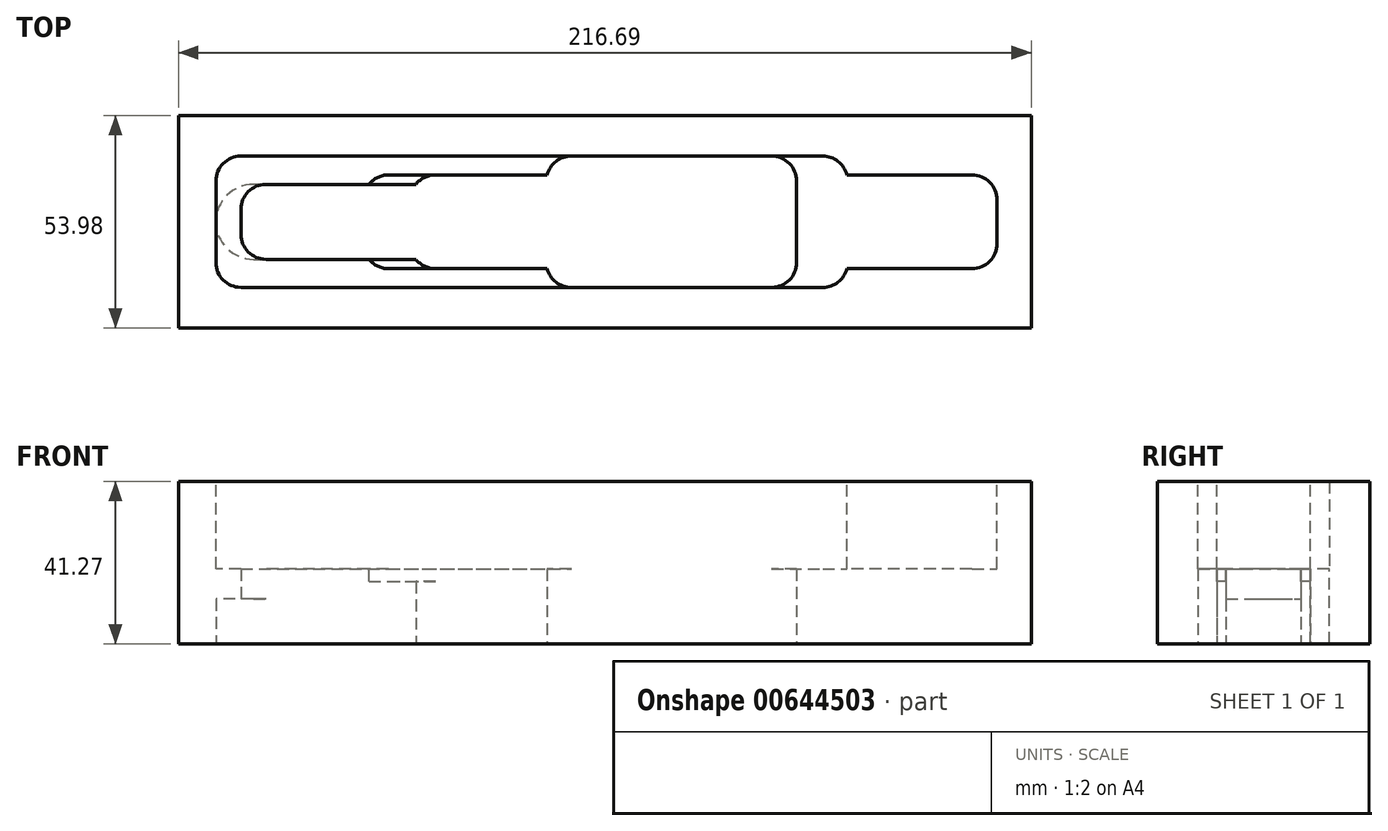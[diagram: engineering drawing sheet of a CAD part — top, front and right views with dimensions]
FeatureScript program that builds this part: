
annotation { "Feature Type Name" : "Feature", "Feature Type Description" : "" }
export const myFeature = defineFeature(function(context is Context, id is Id, definition is map)
    precondition{}
    {
        {
            var Q0;
            Q0=qCreatedBy(makeId("Top.planeOp"),FACE);
            var sketch = newSketch(context, id + "F0", { "sketchPlane" : qUnion([Q0])});
            skLineSegment(sketch, "E0.bottom", {"start": v(127, 26.99) * mm, "end": v(-127, 26.99) * mm});
            skLineSegment(sketch, "E0.top", {"start": v(127, -26.99) * mm, "end": v(-127, -26.99) * mm});
            skLineSegment(sketch, "E0.left", {"start": v(127, 26.99) * mm, "end": v(127, -26.99) * mm});
            skLineSegment(sketch, "E0.right", {"start": v(-127, 26.99) * mm, "end": v(-127, -26.99) * mm});
            skPoint(sketch, "E0.middle", {"position": v(0, 0) * mm});
            skSolve(sketch);
        }
        {
            var Q0;
            Q0=qSketchRegion(id+"F0",true);
            extrude(context, id + "F1", {"entities" : qUnion([Q0]), "depth" : 41.27 * mm});
        }
        {
            var Q0;
            Q0=makeQuery(id+"F1.opExtrude","CAP_FACE",FACE,{"disambiguationData":[OSD([sQuery(id+"F0.wireOp",EDGE,"E0.bottom"),sQuery(id+"F0.wireOp",EDGE,"E0.top"),sQuery(id+"F0.wireOp",EDGE,"E0.left"),sQuery(id+"F0.wireOp",EDGE,"E0.right")])],"isStart":false});
            var sketch = newSketch(context, id + "F2", { "sketchPlane" : qUnion([Q0])});
            skLineSegment(sketch, "E1.bottom", {"start": v(-80.17, -16.67) * mm, "end": v(80.17, -16.67) * mm});
            skLineSegment(sketch, "E1.top", {"start": v(-80.17, 16.67) * mm, "end": v(80.17, 16.67) * mm});
            skLineSegment(sketch, "E1.left", {"start": v(-80.17, -16.67) * mm, "end": v(-80.17, 16.67) * mm});
            skPoint(sketch, "E1.middle", {"position": v(0, 0) * mm});
            skLineSegment(sketch, "E2", {"start": v(80.17, 16.67) * mm, "end": v(80.17, 11.9) * mm});
            skLineSegment(sketch, "E3", {"start": v(80.17, 11.9) * mm, "end": v(118.27, 11.9) * mm});
            skLineSegment(sketch, "E4", {"start": v(118.27, 11.9) * mm, "end": v(118.27, -11.9) * mm});
            skLineSegment(sketch, "E5", {"start": v(118.27, -11.9) * mm, "end": v(80.17, -11.9) * mm});
            skLineSegment(sketch, "E6", {"start": v(80.17, -11.9) * mm, "end": v(80.17, -16.67) * mm});
            skSolve(sketch);
        }
        {
            var Q0;
            Q0=qSketchRegion(id+"F2",true);
            extrude(context, id + "F3", {"entities" : qUnion([Q0]), "operationType" : NewBodyOperationType.REMOVE, "oppositeDirection" : true, "depth" : 22.22 * mm});
        }
        {
            var Q0;
            Q0=makeQuery(id+"F3.boolean.opBoolean","COPY",EDGE,{"derivedFrom":makeQuery(id+"F3.opExtrude","SWEPT_EDGE",EDGE,{"disambiguationData":[OSD([sQuery(id+"F2.wireOp",EDGE,"E1.bottom"),sQuery(id+"F2.wireOp",EDGE,"E1.left")])]})});
            var Q1;
            Q1=makeQuery(id+"F3.boolean.opBoolean","COPY",EDGE,{"derivedFrom":makeQuery(id+"F3.opExtrude","SWEPT_EDGE",EDGE,{"disambiguationData":[OSD([sQuery(id+"F2.wireOp",EDGE,"E4"),sQuery(id+"F2.wireOp",EDGE,"E5")])]})});
            var Q2;
            Q2=makeQuery(id+"F3.boolean.opBoolean","COPY",EDGE,{"derivedFrom":makeQuery(id+"F3.opExtrude","SWEPT_EDGE",EDGE,{"disambiguationData":[OSD([sQuery(id+"F2.wireOp",EDGE,"E3"),sQuery(id+"F2.wireOp",EDGE,"E4")])]})});
            var Q3;
            Q3=makeQuery(id+"F3.boolean.opBoolean","COPY",EDGE,{"derivedFrom":makeQuery(id+"F3.opExtrude","SWEPT_EDGE",EDGE,{"disambiguationData":[OSD([sQuery(id+"F2.wireOp",EDGE,"E1.top"),sQuery(id+"F2.wireOp",EDGE,"E2")])]})});
            var Q4;
            Q4=makeQuery(id+"F3.boolean.opBoolean","COPY",EDGE,{"derivedFrom":makeQuery(id+"F3.opExtrude","SWEPT_EDGE",EDGE,{"disambiguationData":[OSD([sQuery(id+"F2.wireOp",EDGE,"E1.top"),sQuery(id+"F2.wireOp",EDGE,"E1.left")])]})});
            var Q5;
            Q5=makeQuery(id+"F3.boolean.opBoolean","COPY",EDGE,{"derivedFrom":makeQuery(id+"F3.opExtrude","SWEPT_EDGE",EDGE,{"disambiguationData":[OSD([sQuery(id+"F2.wireOp",EDGE,"E1.bottom"),sQuery(id+"F2.wireOp",EDGE,"E6")])]})});
            fillet(context, id + "F4", {"entities" : qUnion([Q0, Q1, Q2, Q3, Q4, Q5]), "radius" : 6.35 * mm, "tangentPropagation" : true, "allowEdgeOverflow" : false});
        }
        {
            var Q0;
            Q0=makeQuery(id+"F1.opExtrude","CAP_FACE",FACE,{"disambiguationData":[OSD([sQuery(id+"F0.wireOp",EDGE,"E0.bottom"),sQuery(id+"F0.wireOp",EDGE,"E0.top"),sQuery(id+"F0.wireOp",EDGE,"E0.left"),sQuery(id+"F0.wireOp",EDGE,"E0.right")])],"isStart":true});
            var sketch = newSketch(context, id + "F5", { "sketchPlane" : qUnion([Q0])});
            skLineSegment(sketch, "E7", {"start": v(-70.64, 9.52) * mm, "end": v(-29.37, 9.52) * mm});
            skLineSegment(sketch, "E8", {"start": v(-29.37, 9.52) * mm, "end": v(-29.37, 11.9) * mm});
            skLineSegment(sketch, "E9", {"start": v(-29.37, 11.9) * mm, "end": v(3.97, 11.9) * mm});
            skLineSegment(sketch, "E10", {"start": v(3.97, 11.9) * mm, "end": v(3.97, 16.67) * mm});
            skLineSegment(sketch, "E11", {"start": v(3.97, 16.67) * mm, "end": v(67.39, 16.67) * mm});
            skLineSegment(sketch, "E12", {"start": v(67.39, 16.67) * mm, "end": v(67.39, -16.67) * mm});
            skLineSegment(sketch, "E13", {"start": v(67.39, -16.67) * mm, "end": v(3.97, -16.67) * mm});
            skLineSegment(sketch, "E14", {"start": v(3.97, -16.67) * mm, "end": v(3.97, -11.9) * mm});
            skLineSegment(sketch, "E15", {"start": v(3.97, -11.9) * mm, "end": v(-29.37, -11.9) * mm});
            skLineSegment(sketch, "E16", {"start": v(-29.37, -11.9) * mm, "end": v(-29.37, -9.53) * mm});
            skLineSegment(sketch, "E17", {"start": v(-29.37, -9.53) * mm, "end": v(-70.64, -9.53) * mm});
            skArc(sketch, "E18", {"start": v(-70.64, 9.52) * mm, "mid": v(-80.17, 0) * mm, "end": v(-70.64, -9.53) * mm});
            skSolve(sketch);
        }
        {
            var Q0;
            Q0=qSketchRegion(id+"F5",true);
            extrude(context, id + "F6", {"entities" : qUnion([Q0]), "operationType" : NewBodyOperationType.REMOVE, "oppositeDirection" : true, "depth" : 11.43 * mm});
        }
        {
            var Q0;
            Q0=makeQuery(id+"F1.opExtrude","CAP_FACE",FACE,{"disambiguationData":[OSD([sQuery(id+"F0.wireOp",EDGE,"E0.bottom"),sQuery(id+"F0.wireOp",EDGE,"E0.top"),sQuery(id+"F0.wireOp",EDGE,"E0.left"),sQuery(id+"F0.wireOp",EDGE,"E0.right")])],"isStart":true});
            var sketch = newSketch(context, id + "F7", { "sketchPlane" : qUnion([Q0])});
            skLineSegment(sketch, "E19", {"start": v(-70.64, 9.52) * mm, "end": v(-29.37, 9.52) * mm});
            skLineSegment(sketch, "E20", {"start": v(-29.37, 9.52) * mm, "end": v(-29.37, 11.9) * mm});
            skLineSegment(sketch, "E21", {"start": v(-29.37, 11.9) * mm, "end": v(3.97, 11.9) * mm});
            skLineSegment(sketch, "E22", {"start": v(3.97, 11.9) * mm, "end": v(3.97, 16.67) * mm});
            skLineSegment(sketch, "E23", {"start": v(3.97, 16.67) * mm, "end": v(67.39, 16.67) * mm});
            skLineSegment(sketch, "E24", {"start": v(67.39, 16.67) * mm, "end": v(67.39, -16.67) * mm});
            skLineSegment(sketch, "E25", {"start": v(67.39, -16.67) * mm, "end": v(3.97, -16.67) * mm});
            skLineSegment(sketch, "E26", {"start": v(3.97, -16.67) * mm, "end": v(3.97, -11.9) * mm});
            skLineSegment(sketch, "E27", {"start": v(3.97, -11.9) * mm, "end": v(-29.37, -11.9) * mm});
            skLineSegment(sketch, "E28", {"start": v(-29.37, -11.9) * mm, "end": v(-29.37, -9.53) * mm});
            skLineSegment(sketch, "E29", {"start": v(-29.37, -9.53) * mm, "end": v(-70.64, -9.53) * mm});
            skArc(sketch, "E30", {"start": v(-70.64, 9.52) * mm, "mid": v(-72.25, 9.39) * mm, "end": v(-73.82, 8.98) * mm});
            skArc(sketch, "E31", {"start": v(-70.64, -9.53) * mm, "mid": v(-72.25, -9.39) * mm, "end": v(-73.82, -8.98) * mm});
            skLineSegment(sketch, "E32", {"start": v(-73.82, 8.98) * mm, "end": v(-73.82, -8.98) * mm});
            skSolve(sketch);
        }
        {
            var Q0;
            Q0=qSketchRegion(id+"F7",true);
            extrude(context, id + "F8", {"entities" : qUnion([Q0]), "operationType" : NewBodyOperationType.REMOVE, "endBound" : BoundingType.THROUGH_ALL, "oppositeDirection" : true, "depth" : 25.4 * mm});
        }
        {
            var Q0;
            Q0=makeQuery(id+"F8.boolean.opBoolean","MERGE",EDGE,{"derivedFrom":[makeQuery(id+"F6.boolean.opBoolean","COPY",EDGE,{"derivedFrom":makeQuery(id+"F6.opExtrude","SWEPT_EDGE",EDGE,{"disambiguationData":[OSD([sQuery(id+"F5.wireOp",EDGE,"E10"),sQuery(id+"F5.wireOp",EDGE,"E11")])]})}),makeQuery(id+"F8.opExtrude","SWEPT_EDGE",EDGE,{"disambiguationData":[OSD([sQuery(id+"F7.wireOp",EDGE,"E22"),sQuery(id+"F7.wireOp",EDGE,"E23")])]})]});
            var Q1;
            Q1=makeQuery(id+"F8.boolean.opBoolean","MERGE",EDGE,{"derivedFrom":[makeQuery(id+"F6.boolean.opBoolean","COPY",EDGE,{"derivedFrom":makeQuery(id+"F6.opExtrude","SWEPT_EDGE",EDGE,{"disambiguationData":[OSD([sQuery(id+"F5.wireOp",EDGE,"E8"),sQuery(id+"F5.wireOp",EDGE,"E9")])]})}),makeQuery(id+"F8.opExtrude","SWEPT_EDGE",EDGE,{"disambiguationData":[OSD([sQuery(id+"F7.wireOp",EDGE,"E20"),sQuery(id+"F7.wireOp",EDGE,"E21")])]})]});
            var Q2;
            Q2=makeQuery(id+"F8.boolean.opBoolean","MERGE",EDGE,{"derivedFrom":[makeQuery(id+"F6.boolean.opBoolean","COPY",EDGE,{"derivedFrom":makeQuery(id+"F6.opExtrude","SWEPT_EDGE",EDGE,{"disambiguationData":[OSD([sQuery(id+"F5.wireOp",EDGE,"E11"),sQuery(id+"F5.wireOp",EDGE,"E12")])]})}),makeQuery(id+"F8.opExtrude","SWEPT_EDGE",EDGE,{"disambiguationData":[OSD([sQuery(id+"F7.wireOp",EDGE,"E23"),sQuery(id+"F7.wireOp",EDGE,"E24")])]})]});
            var Q3;
            Q3=makeQuery(id+"F8.boolean.opBoolean","MERGE",EDGE,{"derivedFrom":[makeQuery(id+"F6.boolean.opBoolean","COPY",EDGE,{"derivedFrom":makeQuery(id+"F6.opExtrude","SWEPT_EDGE",EDGE,{"disambiguationData":[OSD([sQuery(id+"F5.wireOp",EDGE,"E12"),sQuery(id+"F5.wireOp",EDGE,"E13")])]})}),makeQuery(id+"F8.opExtrude","SWEPT_EDGE",EDGE,{"disambiguationData":[OSD([sQuery(id+"F7.wireOp",EDGE,"E24"),sQuery(id+"F7.wireOp",EDGE,"E25")])]})]});
            var Q4;
            Q4=makeQuery(id+"F8.boolean.opBoolean","MERGE",EDGE,{"derivedFrom":[makeQuery(id+"F6.boolean.opBoolean","COPY",EDGE,{"derivedFrom":makeQuery(id+"F6.opExtrude","SWEPT_EDGE",EDGE,{"disambiguationData":[OSD([sQuery(id+"F5.wireOp",EDGE,"E13"),sQuery(id+"F5.wireOp",EDGE,"E14")])]})}),makeQuery(id+"F8.opExtrude","SWEPT_EDGE",EDGE,{"disambiguationData":[OSD([sQuery(id+"F7.wireOp",EDGE,"E25"),sQuery(id+"F7.wireOp",EDGE,"E26")])]})]});
            var Q5;
            Q5=makeQuery(id+"F8.boolean.opBoolean","MERGE",EDGE,{"derivedFrom":[makeQuery(id+"F6.boolean.opBoolean","COPY",EDGE,{"derivedFrom":makeQuery(id+"F6.opExtrude","SWEPT_EDGE",EDGE,{"disambiguationData":[OSD([sQuery(id+"F5.wireOp",EDGE,"E15"),sQuery(id+"F5.wireOp",EDGE,"E16")])]})}),makeQuery(id+"F8.opExtrude","SWEPT_EDGE",EDGE,{"disambiguationData":[OSD([sQuery(id+"F7.wireOp",EDGE,"E27"),sQuery(id+"F7.wireOp",EDGE,"E28")])]})]});
            var Q6;
            Q6=makeQuery(id+"F8.boolean.opBoolean","COPY",EDGE,{"derivedFrom":makeQuery(id+"F8.opExtrude","SWEPT_EDGE",EDGE,{"disambiguationData":[OSD([sQuery(id+"F5.wireOp",EDGE,"E18"),sQuery(id+"F7.wireOp",EDGE,"E31"),sQuery(id+"F7.wireOp",EDGE,"E32")])]})});
            var Q7;
            Q7=makeQuery(id+"F8.boolean.opBoolean","COPY",EDGE,{"derivedFrom":makeQuery(id+"F8.opExtrude","SWEPT_EDGE",EDGE,{"disambiguationData":[OSD([sQuery(id+"F5.wireOp",EDGE,"E18"),sQuery(id+"F7.wireOp",EDGE,"E30"),sQuery(id+"F7.wireOp",EDGE,"E32")])]})});
            fillet(context, id + "F9", {"entities" : qUnion([Q0, Q1, Q2, Q3, Q4, Q5, Q6, Q7]), "radius" : 6.35 * mm, "tangentPropagation" : true, "allowEdgeOverflow" : false});
        }
        {
            var Q0;
            Q0=makeQuery(id+"F1.opExtrude","SWEPT_FACE",FACE,{"disambiguationData":[OSD([sQuery(id+"F0.wireOp",EDGE,"E0.top")])]});
            var sketch = newSketch(context, id + "F10", { "sketchPlane" : qUnion([Q0])});
            skLineSegment(sketch, "E33.bottom", {"start": v(-127, 41.28) * mm, "end": v(-89.7, 41.28) * mm});
            skLineSegment(sketch, "E33.top", {"start": v(-127, 0) * mm, "end": v(-89.7, 0) * mm});
            skLineSegment(sketch, "E33.left", {"start": v(-127, 41.28) * mm, "end": v(-127, 0) * mm});
            skLineSegment(sketch, "E33.right", {"start": v(-89.7, 41.28) * mm, "end": v(-89.7, 0) * mm});
            skSolve(sketch);
        }
        {
            var Q0;
            Q0=qSketchRegion(id+"F10",true);
            extrude(context, id + "F11", {"entities" : qUnion([Q0]), "operationType" : NewBodyOperationType.REMOVE, "endBound" : BoundingType.THROUGH_ALL, "oppositeDirection" : true, "depth" : 25.4 * mm});
        }
        {
            var Q0;
            {var subQ0=sQuery(id+"F2.wireOp",EDGE,"E1.bottom");var subQ1=sQuery(id+"F2.wireOp",EDGE,"E1.left");var subQ2=sQuery(id+"F2.wireOp",EDGE,"E1.top");Q0=makeQuery(id+"F8.boolean.opBoolean","SPLIT",FACE,{"disambiguationData":[TD([makeQuery(id+"F3.boolean.opBoolean","COPY",FACE,{"derivedFrom":makeQuery(id+"F3.opExtrude","SWEPT_FACE",FACE,{"disambiguationData":[OSD([subQ1])]})})])],"derivedFrom":makeQuery(id+"F3.boolean.opBoolean","COPY",FACE,{"derivedFrom":makeQuery(id+"F3.opExtrude","CAP_FACE",FACE,{"disambiguationData":[OSD([subQ0,subQ2,subQ1,sQuery(id+"F2.wireOp",EDGE,"E2"),sQuery(id+"F2.wireOp",EDGE,"E3"),sQuery(id+"F2.wireOp",EDGE,"E4"),sQuery(id+"F2.wireOp",EDGE,"E5"),sQuery(id+"F2.wireOp",EDGE,"E6")])],"isStart":false})})});}
            var sketch = newSketch(context, id + "F12", { "sketchPlane" : qUnion([Q0])});
            skLineSegment(sketch, "E34.bottom", {"start": v(-41.28, 9.53) * mm, "end": v(-22.23, 9.53) * mm});
            skLineSegment(sketch, "E34.top", {"start": v(-41.28, 11.9) * mm, "end": v(-22.23, 11.9) * mm});
            skLineSegment(sketch, "E34.left", {"start": v(-41.28, 9.53) * mm, "end": v(-41.28, 11.9) * mm});
            skLineSegment(sketch, "E34.right", {"start": v(-22.23, 9.53) * mm, "end": v(-22.23, 11.9) * mm});
            skLineSegment(sketch, "E35.MirrorCS", {"start": v(-41.28, -9.53) * mm, "end": v(-22.23, -9.53) * mm});
            skLineSegment(sketch, "E36.MirrorCS", {"start": v(-41.28, -11.9) * mm, "end": v(-22.23, -11.9) * mm});
            skLineSegment(sketch, "E37.MirrorCS", {"start": v(-41.28, -9.53) * mm, "end": v(-41.28, -11.9) * mm});
            skLineSegment(sketch, "E38.MirrorCS", {"start": v(-22.23, -9.53) * mm, "end": v(-22.23, -11.9) * mm});
            skSolve(sketch);
        }
        {
            var Q0;
            Q0=qSketchRegion(id+"F12",true);
            extrude(context, id + "F13", {"entities" : qUnion([Q0]), "operationType" : NewBodyOperationType.REMOVE, "oppositeDirection" : true, "depth" : 3.17 * mm});
        }
        {
            var Q0;
            Q0=makeQuery(id+"F13.boolean.opBoolean","COPY",EDGE,{"derivedFrom":makeQuery(id+"F13.opExtrude","SWEPT_EDGE",EDGE,{"disambiguationData":[OSD([sQuery(id+"F12.wireOp",EDGE,"E34.top"),sQuery(id+"F12.wireOp",EDGE,"E34.left")])]})});
            var Q1;
            Q1=makeQuery(id+"F13.boolean.opBoolean","COPY",EDGE,{"derivedFrom":makeQuery(id+"F13.opExtrude","SWEPT_EDGE",EDGE,{"disambiguationData":[OSD([sQuery(id+"F12.wireOp",EDGE,"E36.MirrorCS"),sQuery(id+"F12.wireOp",EDGE,"E37.MirrorCS")])]})});
            fillet(context, id + "F14", {"entities" : qUnion([Q0, Q1]), "radius" : 6.35 * mm, "tangentPropagation" : true, "allowEdgeOverflow" : false});
        }
    });
